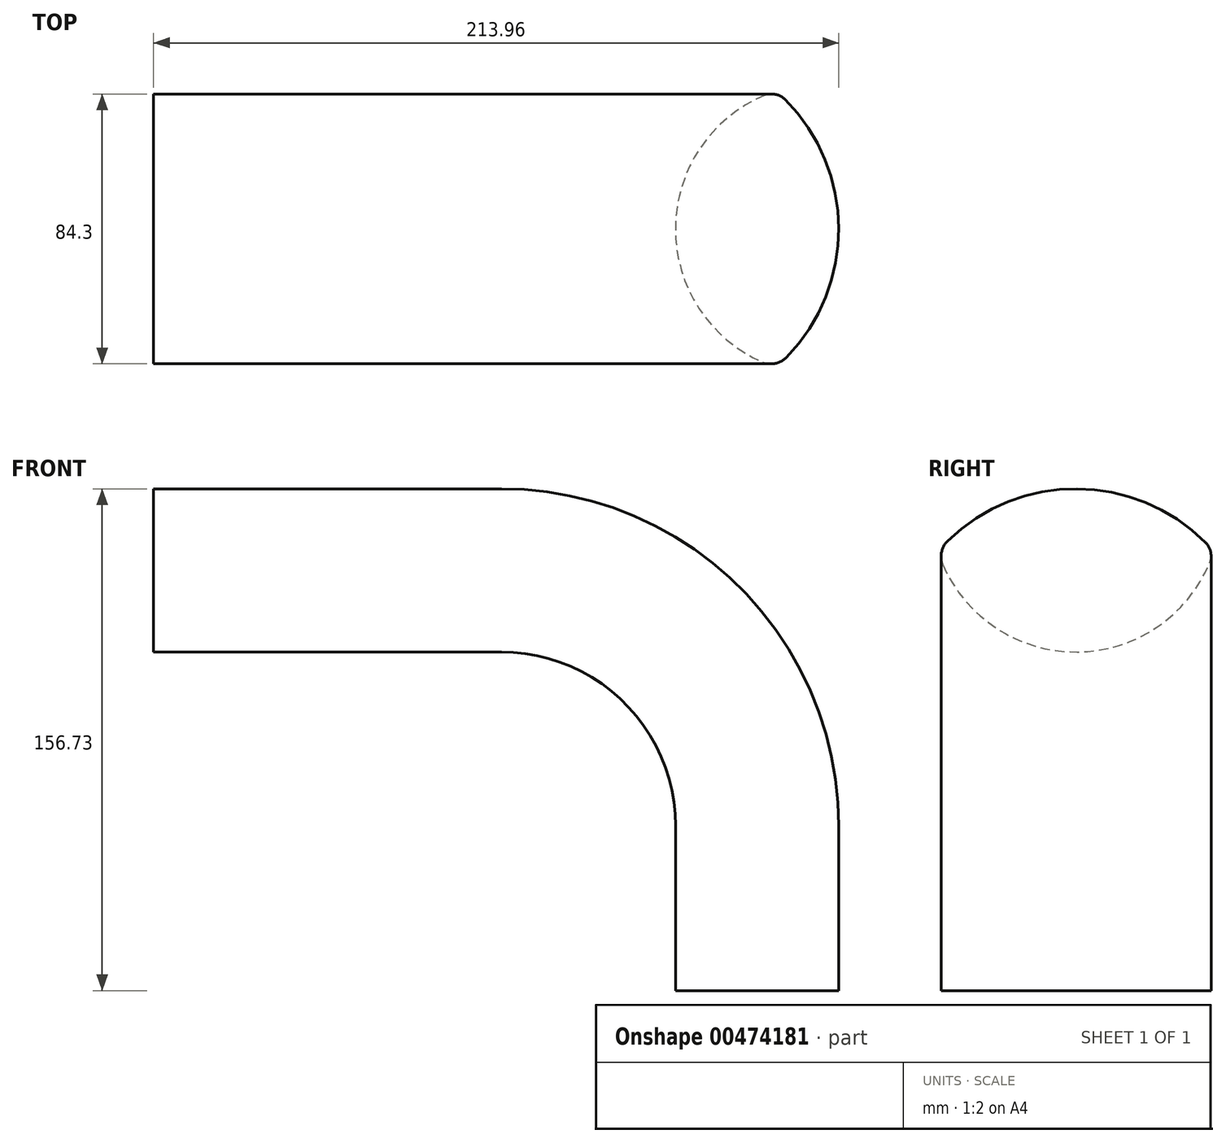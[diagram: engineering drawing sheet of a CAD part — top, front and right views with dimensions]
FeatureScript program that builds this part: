
annotation { "Feature Type Name" : "Feature", "Feature Type Description" : "" }
export const myFeature = defineFeature(function(context is Context, id is Id, definition is map)
    precondition{}
    {
        {
            var Q0;
            Q0=qCreatedBy(makeId("Front.planeOp"),FACE);
            var sketch = newSketch(context, id + "F0", { "sketchPlane" : qUnion([Q0])});
            skLineSegment(sketch, "E0", {"start": v(0, 0) * mm, "end": v(0, 51.46) * mm});
            skLineSegment(sketch, "E1", {"start": v(-99.55, 151) * mm, "end": v(-208.24, 151) * mm});
            skPoint(sketch, "E2.visualSharp", {"position": v(0, 151) * mm});
            skArc(sketch, "E2.filletArc", {"start": v(0, 51.46) * mm, "mid": v(-29.16, 121.85) * mm, "end": v(-99.55, 151) * mm});
            skSolve(sketch);
        }
        {
            var Q0;
            Q0=qCreatedBy(makeId("Top.planeOp"),FACE);
            var sketch = newSketch(context, id + "F1", { "sketchPlane" : qUnion([Q0])});
            skArc(sketch, "E3", {"start": v(-10.64, -40.1) * mm, "mid": v(5.72, 0.3) * mm, "end": v(-11.06, 40.52) * mm});
            skArc(sketch, "E4", {"start": v(-11.06, 40.52) * mm, "mid": v(-14.05, 42.11) * mm, "end": v(-17.43, 41.78) * mm});
            skArc(sketch, "E5", {"start": v(-10.64, -40.1) * mm, "mid": v(-14.1, -41.96) * mm, "end": v(-18, -41.53) * mm});
            skPoint(sketch, "E6.visualSharp", {"position": v(-4.7, -1.87) * mm});
            skArc(sketch, "E7", {"start": v(-17.43, 41.78) * mm, "mid": v(-45.26, 0.3) * mm, "end": v(-18, -41.53) * mm});
            skSolve(sketch);
        }
        {
            var Q0;
            Q0 = qSketchRegion(id + "F1", true);
            var Q1;
            Q1 = qConstructionFilter(qBodyType(qCreatedBy(id + "F0" ,EDGE), BodyType.WIRE), ConstructionObject.NO);
            sweep(context, id + "F2", {"profiles" : qUnion([Q0]), "path" : qUnion([Q1])});
        }
    });
